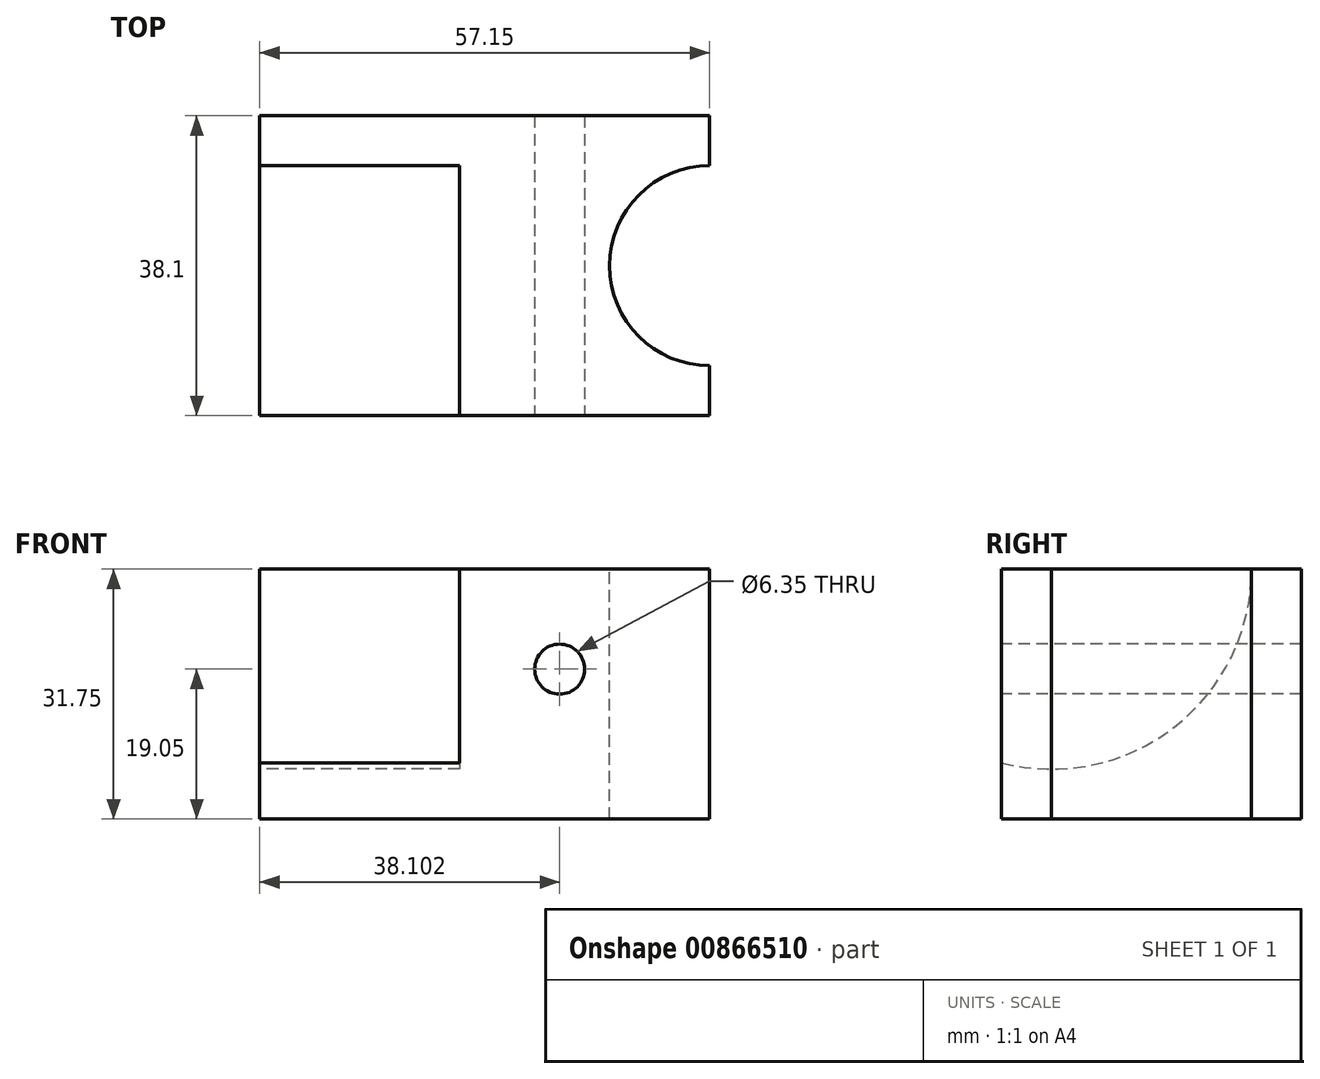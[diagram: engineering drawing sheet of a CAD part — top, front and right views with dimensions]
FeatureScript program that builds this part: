
annotation { "Feature Type Name" : "Feature", "Feature Type Description" : "" }
export const myFeature = defineFeature(function(context is Context, id is Id, definition is map)
    precondition{}
    {
        {
            var Q0;
            Q0=qCreatedBy(makeId("Top.planeOp"),FACE);
            var sketch = newSketch(context, id + "F0", { "sketchPlane" : qUnion([Q0])});
            skLineSegment(sketch, "E0.bottom", {"start": v(13.96, 6.43) * mm, "end": v(71.11, 6.43) * mm});
            skLineSegment(sketch, "E0.top", {"start": v(13.96, -31.67) * mm, "end": v(71.11, -31.67) * mm});
            skLineSegment(sketch, "E0.left", {"start": v(13.96, 6.43) * mm, "end": v(13.96, -31.67) * mm});
            skLineSegment(sketch, "E0.right", {"start": v(71.11, 6.43) * mm, "end": v(71.11, -31.67) * mm});
            skSolve(sketch);
        }
        {
            var Q0;
            Q0 = qSketchRegion(id + "F0", true);
            extrude(context, id + "F1", {"entities" : qUnion([Q0]), "depth" : 31.75 * mm, "offsetDistance" : 25.4 * mm});
        }
        {
            var Q0;
            Q0=makeQuery(id+"F1.opExtrude","CAP_FACE",FACE,{"disambiguationData":[OSD([sQuery(id+"F0.wireOp",EDGE,"E0.bottom"),sQuery(id+"F0.wireOp",EDGE,"E0.top"),sQuery(id+"F0.wireOp",EDGE,"E0.left"),sQuery(id+"F0.wireOp",EDGE,"E0.right")])],"isStart":false});
            var sketch = newSketch(context, id + "F2", { "sketchPlane" : qUnion([Q0])});
            skCircle(sketch, "E1", {"center": v(71.11, -12.62) * mm, "radius": 12.7 * mm});
            skSolve(sketch);
        }
        {
            var Q0;
            {var subQ0=sQuery(id+"F2.wireOp",EDGE,"E1");var subQ1=makeQuery(id+"F1.opExtrude","CAP_EDGE",EDGE,{"disambiguationData":[OSD([sQuery(id+"F0.wireOp",EDGE,"E0.right")])],"isStart":false});var subQ2=makeQuery(id+"F2.imprint","INTERSECT",VERTEX,{"disambiguationData":[OD(0.0)],"derivedFrom":[subQ1,subQ0]});Q0=makeQuery(id+"F2.imprint","IMPRINT",FACE,{"disambiguationData":[TD([[makeQuery(id+"F2.imprint","IMPRINT",EDGE,{"disambiguationData":[TD([[subQ2,1.0]])],"derivedFrom":subQ0}),1.0]])]});}
            var Q1;
            {var subQ0=sQuery(id+"F2.wireOp",EDGE,"E1");var subQ1=makeQuery(id+"F1.opExtrude","CAP_EDGE",EDGE,{"disambiguationData":[OSD([sQuery(id+"F0.wireOp",EDGE,"E0.right")])],"isStart":false});var subQ2=makeQuery(id+"F2.imprint","INTERSECT",VERTEX,{"disambiguationData":[OD(0.0)],"derivedFrom":[subQ1,subQ0]});Q1=makeQuery(id+"F2.imprint","IMPRINT",FACE,{"disambiguationData":[TD([[makeQuery(id+"F2.imprint","IMPRINT",EDGE,{"disambiguationData":[TD([[subQ2,-1.0]])],"derivedFrom":subQ0}),1.0]])]});}
            var Q2;
            Q2=sQuery(id+"F2.wireOp",EDGE,"E1");
            extrude(context, id + "F3", {"entities" : qUnion([Q0, Q1]), "operationType" : NewBodyOperationType.REMOVE, "surfaceEntities" : qUnion([Q2]), "oppositeDirection" : true, "depth" : 31.75 * mm, "offsetDistance" : 25.4 * mm});
        }
        {
            var Q0;
            Q0=makeQuery(id+"F1.opExtrude","SWEPT_FACE",FACE,{"disambiguationData":[OSD([sQuery(id+"F0.wireOp",EDGE,"E0.top")])]});
            var sketch = newSketch(context, id + "F4", { "sketchPlane" : qUnion([Q0])});
            skCircle(sketch, "E2", {"center": v(52.06, 19.05) * mm, "radius": 3.18 * mm});
            skSolve(sketch);
        }
        {
            var Q0;
            Q0 = qSketchRegion(id + "F4", true);
            extrude(context, id + "F5", {"entities" : qUnion([Q0]), "operationType" : NewBodyOperationType.REMOVE, "oppositeDirection" : true, "depth" : 37.85 * mm, "offsetDistance" : 25.4 * mm});
        }
        {
            var Q0;
            Q0 = qSketchRegion(id + "F4", true);
            extrude(context, id + "F6", {"entities" : qUnion([Q0]), "operationType" : NewBodyOperationType.REMOVE, "oppositeDirection" : true, "depth" : 38.1 * mm, "offsetDistance" : 25.4 * mm});
        }
        {
            var Q0;
            Q0=makeQuery(id+"F1.opExtrude","SWEPT_FACE",FACE,{"disambiguationData":[OSD([sQuery(id+"F0.wireOp",EDGE,"E0.left")])]});
            var sketch = newSketch(context, id + "F7", { "sketchPlane" : qUnion([Q0])});
            skPoint(sketch, "E3.0.midPoint", {"position": v(50.72, 31.75) * mm});
            skCircle(sketch, "E4", {"center": v(25.32, 31.75) * mm, "radius": 25.4 * mm});
            skSolve(sketch);
        }
        {
            var Q0;
            Q0 = qSketchRegion(id + "F7", true);
            extrude(context, id + "F8", {"entities" : qUnion([Q0]), "operationType" : NewBodyOperationType.REMOVE, "oppositeDirection" : true, "depth" : 25.4 * mm, "offsetDistance" : 25.4 * mm});
        }
    });
